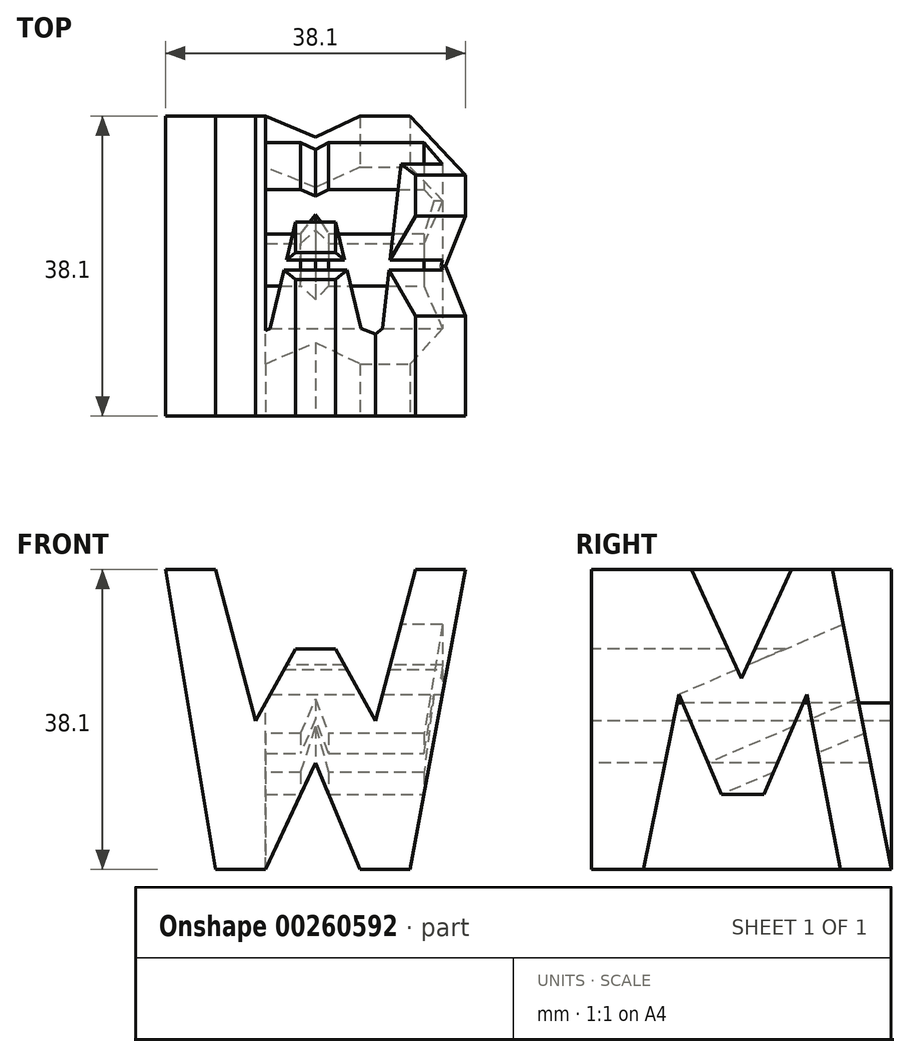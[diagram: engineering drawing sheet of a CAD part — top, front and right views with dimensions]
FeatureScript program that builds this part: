
annotation { "Feature Type Name" : "Feature", "Feature Type Description" : "" }
export const myFeature = defineFeature(function(context is Context, id is Id, definition is map)
    precondition{}
    {
        {
            var Q0;
            Q0=qCreatedBy(makeId("Front.planeOp"),FACE);
            var sketch = newSketch(context, id + "F0", { "sketchPlane" : qUnion([Q0])});
            skLineSegment(sketch, "E0", {"start": v(0, 38.1) * mm, "end": v(0, 0) * mm});
            skLineSegment(sketch, "E1", {"start": v(0, 0) * mm, "end": v(38.1, 0) * mm});
            skLineSegment(sketch, "E2", {"start": v(38.1, 0) * mm, "end": v(38.1, 38.1) * mm});
            skLineSegment(sketch, "E3", {"start": v(38.1, 38.1) * mm, "end": v(0, 38.1) * mm});
            skSolve(sketch);
        }
        {
            var Q0;
            Q0 = qSketchRegion(id + "F0", true);
            extrude(context, id + "F1", {"entities" : qUnion([Q0]), "depth" : 38.1 * mm});
        }
        {
            var Q0;
            Q0=qCreatedBy(makeId("Front.planeOp"),FACE);
            cPlane(context, id + "F2", {"entities" : qUnion([Q0]), "cplaneType" : CPlaneType.OFFSET, "offset" : 38.1 * mm, "width" : 152.4 * mm, "height" : 152.4 * mm});
        }
        {
            var Q0;
            Q0=qCreatedBy(makeId("Right.planeOp"),FACE);
            cPlane(context, id + "F3", {"entities" : qUnion([Q0]), "cplaneType" : CPlaneType.OFFSET, "offset" : 38.1 * mm, "width" : 152.4 * mm, "height" : 152.4 * mm});
        }
        {
            var Q0;
            Q0 = qSketchRegion(id + "F0", true);
            extrude(context, id + "F4", {"entities" : qUnion([Q0]), "operationType" : NewBodyOperationType.ADD, "depth" : 38.1 * mm});
        }
        {
            var Q0;
            Q0=qCreatedBy(id+"F3.planeOp",FACE);
            var sketch = newSketch(context, id + "F5", { "sketchPlane" : qUnion([Q0])});
            skLineSegment(sketch, "E4", {"start": v(0, 0) * mm, "end": v(0, 38.1) * mm});
            skLineSegment(sketch, "E5", {"start": v(0, 38.1) * mm, "end": v(-38.1, 38.1) * mm});
            skLineSegment(sketch, "E6", {"start": v(-38.1, 38.1) * mm, "end": v(-38.1, 0) * mm});
            skLineSegment(sketch, "E7", {"start": v(-38.1, 0) * mm, "end": v(0, 0) * mm});
            skSolve(sketch);
        }
        {
            var Q0;
            Q0=makeQuery(id+"F1.opExtrude","CAP_FACE",FACE,{"disambiguationData":[OSD([sQuery(id+"F0.wireOp",EDGE,"E0"),sQuery(id+"F0.wireOp",EDGE,"E1"),sQuery(id+"F0.wireOp",EDGE,"E2"),sQuery(id+"F0.wireOp",EDGE,"E3")])],"isStart":false});
            var sketch = newSketch(context, id + "F6", { "sketchPlane" : qUnion([Q0])});
            skLineSegment(sketch, "E8", {"start": v(0, 38.1) * mm, "end": v(6.35, 0) * mm});
            skLineSegment(sketch, "E9", {"start": v(38.1, 38.1) * mm, "end": v(31.08, 0) * mm});
            skLineSegment(sketch, "E10", {"start": v(12.7, 0) * mm, "end": v(19.05, 13.53) * mm});
            skPoint(sketch, "E10.endSnap0", {"position": v(19.05, 0) * mm});
            skLineSegment(sketch, "E11", {"start": v(19.05, 13.53) * mm, "end": v(24.73, 0) * mm});
            skLineSegment(sketch, "E12", {"start": v(6.35, 38.1) * mm, "end": v(11.43, 18.9) * mm});
            skLineSegment(sketch, "E13", {"start": v(11.43, 18.9) * mm, "end": v(16.51, 28) * mm});
            skLineSegment(sketch, "E14", {"start": v(16.51, 28) * mm, "end": v(21.6, 28) * mm});
            skLineSegment(sketch, "E15", {"start": v(21.6, 28) * mm, "end": v(26.67, 18.9) * mm});
            skLineSegment(sketch, "E16", {"start": v(26.67, 18.9) * mm, "end": v(31.75, 38.1) * mm});
            skSolve(sketch);
        }
        {
            var Q0;
            {var subQ0=sQuery(id+"F6.wireOp",EDGE,"E12");Q0=makeQuery(id+"F6.imprint","IMPRINT",FACE,{"disambiguationData":[TD([[makeQuery(id+"F6.imprint","IMPRINT",EDGE,{"derivedFrom":subQ0}),1.0]])]});}
            var Q1;
            {var subQ0=sQuery(id+"F6.wireOp",EDGE,"E8");Q1=makeQuery(id+"F6.imprint","IMPRINT",FACE,{"disambiguationData":[TD([[makeQuery(id+"F6.imprint","IMPRINT",EDGE,{"derivedFrom":subQ0}),-1.0]])]});}
            var Q2;
            {var subQ0=sQuery(id+"F6.wireOp",EDGE,"E10");Q2=makeQuery(id+"F6.imprint","IMPRINT",FACE,{"disambiguationData":[TD([[makeQuery(id+"F6.imprint","IMPRINT",EDGE,{"derivedFrom":subQ0}),-1.0]])]});}
            var Q3;
            {var subQ0=sQuery(id+"F6.wireOp",EDGE,"E9");Q3=makeQuery(id+"F6.imprint","IMPRINT",FACE,{"disambiguationData":[TD([[makeQuery(id+"F6.imprint","IMPRINT",EDGE,{"derivedFrom":subQ0}),1.0]])]});}
            extrude(context, id + "F7", {"entities" : qUnion([Q0, Q1, Q2, Q3]), "operationType" : NewBodyOperationType.REMOVE, "oppositeDirection" : true, "depth" : 25.4 * mm});
        }
        {
            var Q0;
            Q0=makeQuery(id+"F7.boolean.opBoolean","COPY",FACE,{"derivedFrom":makeQuery(id+"F7.opExtrude","CAP_FACE",FACE,{"disambiguationData":[OSD([sQuery(id+"F0.wireOp",EDGE,"E0"),sQuery(id+"F0.wireOp",EDGE,"E1"),sQuery(id+"F6.wireOp",EDGE,"E8")])],"isStart":false})});
            var Q1;
            Q1=makeQuery(id+"F7.boolean.opBoolean","COPY",FACE,{"derivedFrom":makeQuery(id+"F7.opExtrude","CAP_FACE",FACE,{"disambiguationData":[OSD([sQuery(id+"F0.wireOp",EDGE,"E3"),sQuery(id+"F6.wireOp",EDGE,"E12"),sQuery(id+"F6.wireOp",EDGE,"E13"),sQuery(id+"F6.wireOp",EDGE,"E14"),sQuery(id+"F6.wireOp",EDGE,"E15"),sQuery(id+"F6.wireOp",EDGE,"E16")])],"isStart":false})});
            var Q2;
            Q2=makeQuery(id+"F7.boolean.opBoolean","COPY",FACE,{"derivedFrom":makeQuery(id+"F7.opExtrude","CAP_FACE",FACE,{"disambiguationData":[OSD([sQuery(id+"F0.wireOp",EDGE,"E1"),sQuery(id+"F6.wireOp",EDGE,"E10"),sQuery(id+"F6.wireOp",EDGE,"E11")])],"isStart":false})});
            var Q3;
            Q3=makeQuery(id+"F7.boolean.opBoolean","COPY",FACE,{"derivedFrom":makeQuery(id+"F7.opExtrude","CAP_FACE",FACE,{"disambiguationData":[OSD([sQuery(id+"F0.wireOp",EDGE,"E1"),sQuery(id+"F0.wireOp",EDGE,"E2"),sQuery(id+"F6.wireOp",EDGE,"E9")])],"isStart":false})});
            extrude(context, id + "F8", {"entities" : qUnion([Q0, Q1, Q2, Q3]), "operationType" : NewBodyOperationType.REMOVE, "oppositeDirection" : true, "depth" : 25.4 * mm});
        }
        {
            var Q0;
            Q0=qCreatedBy(id+"F3.planeOp",FACE);
            var sketch = newSketch(context, id + "F9", { "sketchPlane" : qUnion([Q0])});
            skLineSegment(sketch, "E17", {"start": v(0, 0) * mm, "end": v(0, 38.1) * mm});
            skLineSegment(sketch, "E18", {"start": v(0, 38.1) * mm, "end": v(-38.1, 38.1) * mm});
            skLineSegment(sketch, "E19", {"start": v(-38.1, 38.1) * mm, "end": v(-38.1, 0) * mm});
            skLineSegment(sketch, "E20", {"start": v(-38.1, 0) * mm, "end": v(0, 0) * mm});
            skLineSegment(sketch, "E21", {"start": v(0, 0) * mm, "end": v(-7.46, 38.1) * mm});
            skLineSegment(sketch, "E22", {"start": v(-38.1, 0) * mm, "end": v(-31.75, 38.1) * mm});
            skLineSegment(sketch, "E23", {"start": v(-25.4, 38.1) * mm, "end": v(-19.05, 24.26) * mm});
            skLineSegment(sketch, "E24", {"start": v(-19.05, 24.26) * mm, "end": v(-12.7, 38.1) * mm});
            skLineSegment(sketch, "E25", {"start": v(-31.75, 0) * mm, "end": v(-26.67, 30.48) * mm});
            skLineSegment(sketch, "E26", {"start": v(-26.67, 30.48) * mm, "end": v(-21.59, 20.73) * mm});
            skLineSegment(sketch, "E27", {"start": v(-21.59, 20.73) * mm, "end": v(-16.5, 20.73) * mm});
            skLineSegment(sketch, "E28", {"start": v(-16.5, 20.73) * mm, "end": v(-11.43, 30.48) * mm});
            skLineSegment(sketch, "E29", {"start": v(-11.43, 30.48) * mm, "end": v(-6.35, 0) * mm});
            skSolve(sketch);
        }
        {
            var Q0;
            Q0=qCreatedBy(id+"F3.planeOp",FACE);
            var sketch = newSketch(context, id + "F10", { "sketchPlane" : qUnion([Q0])});
            skLineSegment(sketch, "E30", {"start": v(-38.1, 0) * mm, "end": v(-31.57, 38.49) * mm});
            skLineSegment(sketch, "E31", {"start": v(-25.35, 36.36) * mm, "end": v(-19.23, 22.23) * mm});
            skLineSegment(sketch, "E32", {"start": v(-19.23, 22.23) * mm, "end": v(-12.86, 36.36) * mm});
            skLineSegment(sketch, "E33", {"start": v(0, 0) * mm, "end": v(-7.68, 38.03) * mm});
            skLineSegment(sketch, "E34", {"start": v(-31.48, 0) * mm, "end": v(-27, 22.22) * mm});
            skLineSegment(sketch, "E35", {"start": v(-27, 22.22) * mm, "end": v(-21.58, 9.52) * mm});
            skLineSegment(sketch, "E36", {"start": v(-21.58, 9.52) * mm, "end": v(-16.16, 9.52) * mm});
            skLineSegment(sketch, "E37", {"start": v(-16.16, 9.52) * mm, "end": v(-10.74, 22.22) * mm});
            skLineSegment(sketch, "E38", {"start": v(-10.74, 22.22) * mm, "end": v(-6.5, 0) * mm});
            skLineSegment(sketch, "E39", {"start": v(-38.1, 0) * mm, "end": v(-38.1, 38.1) * mm});
            skLineSegment(sketch, "E40", {"start": v(-38.1, 38.1) * mm, "end": v(0, 38.1) * mm});
            skLineSegment(sketch, "E41", {"start": v(0, 38.1) * mm, "end": v(0, 0) * mm});
            skLineSegment(sketch, "E42", {"start": v(-38.1, 0) * mm, "end": v(0, 0) * mm});
            skSolve(sketch);
        }
        {
            var Q0;
            {var subQ0=sQuery(id+"F10.wireOp",EDGE,"E34");Q0=makeQuery(id+"F10.imprint","IMPRINT",FACE,{"disambiguationData":[TD([[makeQuery(id+"F10.imprint","IMPRINT",EDGE,{"derivedFrom":subQ0}),-1.0]])]});}
            var Q1;
            {var subQ0=sQuery(id+"F9.wireOp",EDGE,"E23");Q1=makeQuery(id+"F9.imprint","IMPRINT",FACE,{"disambiguationData":[TD([[makeQuery(id+"F9.imprint","IMPRINT",EDGE,{"derivedFrom":subQ0}),1.0]])]});}
            var Q2;
            {var subQ0=sQuery(id+"F9.wireOp",EDGE,"E17");Q2=makeQuery(id+"F9.imprint","IMPRINT",FACE,{"disambiguationData":[TD([[makeQuery(id+"F9.imprint","IMPRINT",EDGE,{"derivedFrom":subQ0}),1.0]])]});}
            extrude(context, id + "F11", {"entities" : qUnion([Q0, Q1, Q2]), "operationType" : NewBodyOperationType.REMOVE, "oppositeDirection" : true, "depth" : 25.4 * mm});
        }
        {
            var Q0;
            Q0=qCreatedBy(makeId("Top.planeOp"),FACE);
            var sketch = newSketch(context, id + "F12", { "sketchPlane" : qUnion([Q0])});
            skLineSegment(sketch, "E43", {"start": v(0, 0) * mm, "end": v(0, -38.1) * mm});
            skLineSegment(sketch, "E44", {"start": v(0, -38.1) * mm, "end": v(38.1, -38.1) * mm});
            skLineSegment(sketch, "E45", {"start": v(38.1, -38.1) * mm, "end": v(38.1, 0) * mm});
            skLineSegment(sketch, "E46", {"start": v(38.1, -22.86) * mm, "end": v(13.53, -22.86) * mm});
            skLineSegment(sketch, "E47", {"start": v(13.53, -22.86) * mm, "end": v(13.53, -30.48) * mm});
            skLineSegment(sketch, "E48", {"start": v(13.53, -30.48) * mm, "end": v(38.1, -30.48) * mm});
            skLineSegment(sketch, "E49", {"start": v(0, -7.62) * mm, "end": v(24.26, -7.62) * mm});
            skLineSegment(sketch, "E50", {"start": v(24.26, -7.62) * mm, "end": v(24.26, -15.24) * mm});
            skSolve(sketch);
        }
        {
            var Q0;
            {var subQ0=sQuery(id+"F12.wireOp",EDGE,"E46");Q0=makeQuery(id+"F12.imprint","IMPRINT",FACE,{"disambiguationData":[TD([[makeQuery(id+"F12.imprint","IMPRINT",EDGE,{"derivedFrom":subQ0}),1.0]])]});}
            extrude(context, id + "F13", {"entities" : qUnion([Q0]), "operationType" : NewBodyOperationType.REMOVE, "oppositeDirection" : true, "depth" : 25.4 * mm});
        }
        {
            var Q0;
            Q0=makeQuery(id+"F11.boolean.opBoolean","COPY",FACE,{"derivedFrom":makeQuery(id+"F11.opExtrude","SWEPT_FACE",FACE,{"disambiguationData":[OSD([sQuery(id+"F10.wireOp",EDGE,"E35")])]})});
            extrude(context, id + "F14", {"entities" : qUnion([Q0]), "operationType" : NewBodyOperationType.REMOVE, "oppositeDirection" : true, "depth" : 25.4 * mm});
        }
    });
